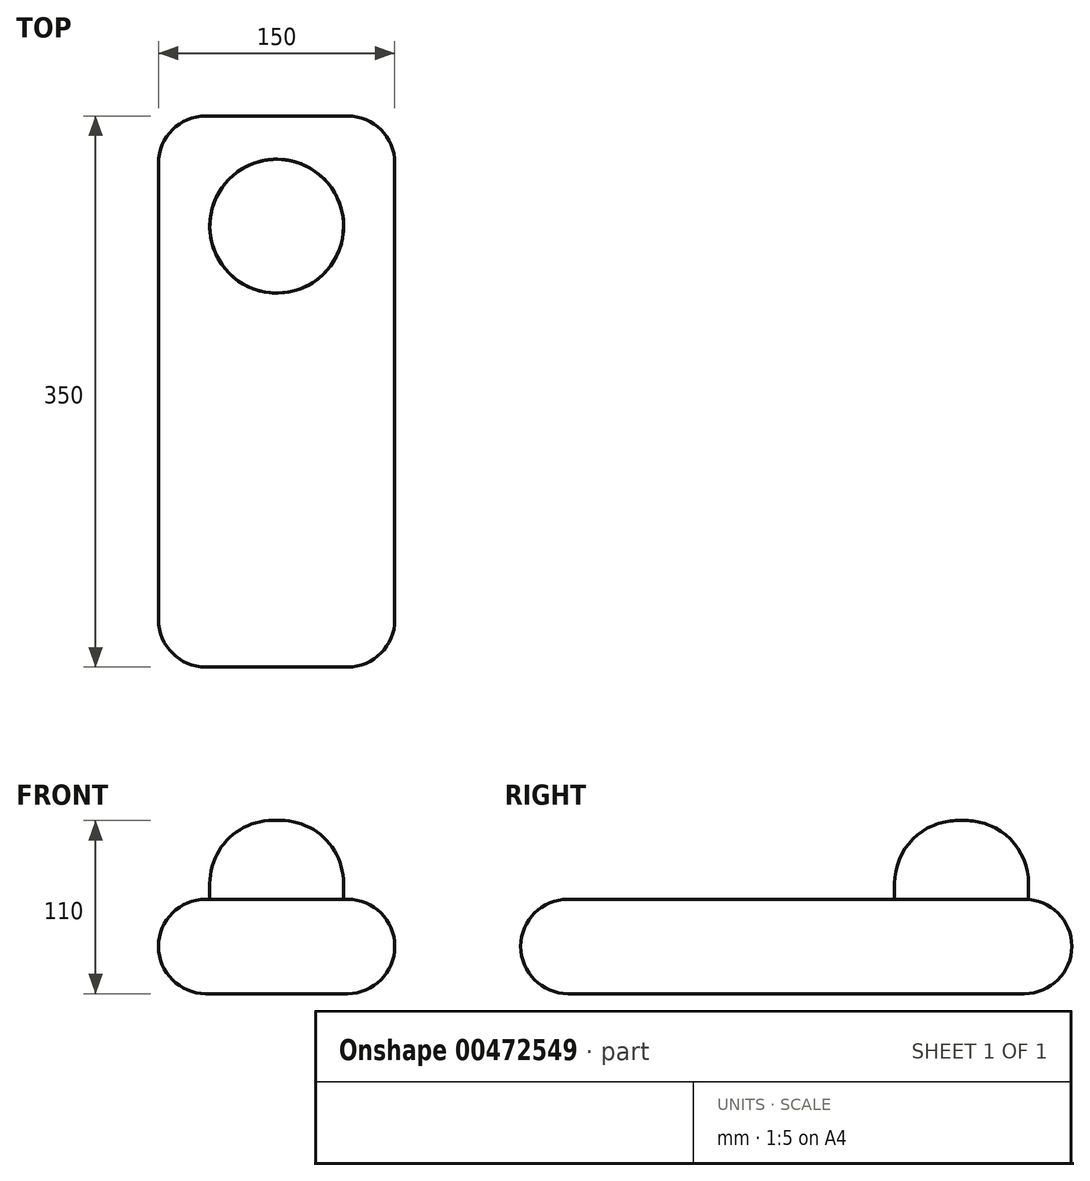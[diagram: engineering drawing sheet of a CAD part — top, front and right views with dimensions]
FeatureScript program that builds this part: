
annotation { "Feature Type Name" : "Feature", "Feature Type Description" : "" }
export const myFeature = defineFeature(function(context is Context, id is Id, definition is map)
    precondition{}
    {
        {
            var Q0;
            Q0=qCreatedBy(makeId("Top.planeOp"),FACE);
            var sketch = newSketch(context, id + "F0", { "sketchPlane" : qUnion([Q0])});
            skLineSegment(sketch, "E0.bottom", {"start": v(-350, 70) * mm, "end": v(-200, 70) * mm});
            skLineSegment(sketch, "E0.top", {"start": v(-350, -280) * mm, "end": v(-200, -280) * mm});
            skLineSegment(sketch, "E0.left", {"start": v(-350, 70) * mm, "end": v(-350, -280) * mm});
            skLineSegment(sketch, "E0.right", {"start": v(-200, 70) * mm, "end": v(-200, -280) * mm});
            skLineSegment(sketch, "E1", {"start": v(0, 253.57) * mm, "end": v(0, -455.94) * mm, "construction": true});
            skSolve(sketch);
        }
        {
            var Q0;
            Q0=makeQuery(id+"F0.imprint","IMPRINT",FACE,{"disambiguationData":[TD([[makeQuery(id+"F0.imprint","IMPRINT",EDGE,{"derivedFrom":sQuery(id+"F0.wireOp",EDGE,"E0.bottom")}),-1.0]])]});
            var Q1;
            Q1=makeQuery(id+"F0.imprint","IMPRINT",FACE,{"disambiguationData":[TD([[makeQuery(id+"F0.imprint","IMPRINT",EDGE,{"derivedFrom":sQuery(id+"F0.wireOp",EDGE,"870aeec5-c2a5-4020-9514-633b8d1ce7c30.MirrorCS")}),1.0]])]});
            extrude(context, id + "F1", {"entities" : qUnion([Q0, Q1]), "depth" : 60 * mm});
        }
        {
            var Q0;
            Q0=makeQuery(id+"F1.opExtrude","SWEPT_EDGE",EDGE,{"disambiguationData":[OSD([sQuery(id+"F0.wireOp",EDGE,"E0.top"),sQuery(id+"F0.wireOp",EDGE,"E0.left")])]});
            var Q1;
            Q1=makeQuery(id+"F1.opExtrude","SWEPT_EDGE",EDGE,{"disambiguationData":[OSD([sQuery(id+"F0.wireOp",EDGE,"E0.top"),sQuery(id+"F0.wireOp",EDGE,"E0.right")])]});
            var Q2;
            Q2=makeQuery(id+"F1.opExtrude","SWEPT_EDGE",EDGE,{"disambiguationData":[OSD([sQuery(id+"F0.wireOp",EDGE,"E0.bottom"),sQuery(id+"F0.wireOp",EDGE,"E0.left")])]});
            var Q3;
            Q3=makeQuery(id+"F1.opExtrude","SWEPT_EDGE",EDGE,{"disambiguationData":[OSD([sQuery(id+"F0.wireOp",EDGE,"E0.bottom"),sQuery(id+"F0.wireOp",EDGE,"E0.right")])]});
            var Q4;
            Q4=makeQuery(id+"F1.opExtrude","CAP_FACE",FACE,{"disambiguationData":[OSD([sQuery(id+"F0.wireOp",EDGE,"E0.bottom"),sQuery(id+"F0.wireOp",EDGE,"E0.top"),sQuery(id+"F0.wireOp",EDGE,"E0.left"),sQuery(id+"F0.wireOp",EDGE,"E0.right")])],"isStart":false});
            var Q5;
            Q5=makeQuery(id+"F1.opExtrude","CAP_FACE",FACE,{"disambiguationData":[OSD([sQuery(id+"F0.wireOp",EDGE,"E0.bottom"),sQuery(id+"F0.wireOp",EDGE,"E0.top"),sQuery(id+"F0.wireOp",EDGE,"E0.left"),sQuery(id+"F0.wireOp",EDGE,"E0.right")])],"isStart":true});
            fillet(context, id + "F2", {"entities" : qUnion([Q0, Q1, Q2, Q3, Q4, Q5]), "radius" : 30 * mm, "tangentPropagation" : true, "allowEdgeOverflow" : false});
        }
        {
            var Q0;
            Q0=makeQuery(id+"F1.opExtrude","CAP_FACE",FACE,{"disambiguationData":[OSD([sQuery(id+"F0.wireOp",EDGE,"E0.bottom"),sQuery(id+"F0.wireOp",EDGE,"E0.top"),sQuery(id+"F0.wireOp",EDGE,"E0.left"),sQuery(id+"F0.wireOp",EDGE,"E0.right")])],"isStart":false});
            var sketch = newSketch(context, id + "F3", { "sketchPlane" : qUnion([Q0])});
            skCircle(sketch, "E2", {"center": v(-275, 0) * mm, "radius": 42.5 * mm});
            skPoint(sketch, "E2.centerSnap0", {"position": v(-275, 40) * mm});
            skLineSegment(sketch, "E3.0", {"start": v(-230, 40) * mm, "end": v(-260.64, 40) * mm});
            skLineSegment(sketch, "E4.trimOffspring", {"start": v(-289.36, 40) * mm, "end": v(-320, 40) * mm});
            skSolve(sketch);
        }
        {
            var Q0;
            {var subQ0=sQuery(id+"F3.wireOp",EDGE,"E2");var subQ1=sQuery(id+"F0.wireOp",EDGE,"E0.bottom");var subQ2=makeQuery(id+"F2.opFillet","BLEND_EDGE",EDGE,{"blendedFrom":[makeQuery(id+"F1.opExtrude","CAP_EDGE",EDGE,{"disambiguationData":[OSD([subQ1])],"isStart":false}),makeQuery(id+"F1.opExtrude","CAP_FACE",FACE,{"disambiguationData":[OSD([subQ1,sQuery(id+"F0.wireOp",EDGE,"E0.top"),sQuery(id+"F0.wireOp",EDGE,"E0.left"),sQuery(id+"F0.wireOp",EDGE,"E0.right")])],"isStart":false})],"blendedInto":[makeQuery(id+"F1.opExtrude","CAP_FACE",FACE,{"disambiguationData":[OSD([subQ1,sQuery(id+"F0.wireOp",EDGE,"E0.top"),sQuery(id+"F0.wireOp",EDGE,"E0.left"),sQuery(id+"F0.wireOp",EDGE,"E0.right")])],"isStart":false})]});var subQ3=makeQuery(id+"F3.imprint","INTERSECT",VERTEX,{"disambiguationData":[OD(0.0)],"derivedFrom":[subQ2,subQ0]});Q0=makeQuery(id+"F3.imprint","IMPRINT",FACE,{"disambiguationData":[TD([[makeQuery(id+"F3.imprint","IMPRINT",EDGE,{"disambiguationData":[TD([[subQ3,-1.0]])],"derivedFrom":subQ0}),1.0]])]});}
            extrude(context, id + "F4", {"entities" : qUnion([Q0]), "operationType" : NewBodyOperationType.ADD, "depth" : 50 * mm, "hasSecondDirection" : true, "secondDirectionOppositeDirection" : true, "secondDirectionDepth" : 25 * mm});
        }
        {
            var Q0;
            Q0=makeQuery(id+"F4.opExtrude","CAP_EDGE",EDGE,{"disambiguationData":[OSD([sQuery(id+"F3.wireOp",EDGE,"E2")])],"isStart":false});
            fillet(context, id + "F5", {"entities" : qUnion([Q0]), "radius" : 40 * mm, "tangentPropagation" : true, "allowEdgeOverflow" : false});
        }
    });
